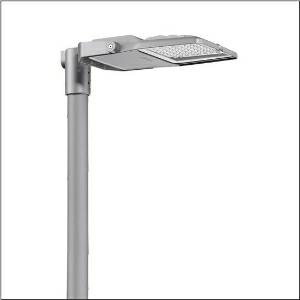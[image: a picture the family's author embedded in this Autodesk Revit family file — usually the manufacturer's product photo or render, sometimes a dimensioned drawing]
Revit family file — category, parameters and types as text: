
# Revit family: floodlight_fl_21_mini___pl52_5xa7775b2d3a_6ba7
name_source: partatom
category: Lighting Fixtures
units: mm (PartAtom-declared; Revit-internal decimal feet)

## family parameters
Cut with Voids When Loaded = No
Host = Face
Light Source = No
Part Type = Normal
Room Calculation Point = No
Round Connector Dimension = Use Diameter
Shared = No

## types (1)
- --- (1 x LED, 6230 lm, 45.7 W, 3000K)
    Apparent Load = 46 VA
    CIE Flux Codes = 26 60 98 100 100
    Color Rendering = 70
    Color Temperature = 3000K
    Default Elevation = 1800 mm
    Description = Floodlight FL 21 mini, floodlight, primary light control with lens, of PMMA, primary optical cover: protective disc, of toughened safety glass, transparent, light distribution: PL52, light emission: direct distribution, installation type: surface-mounted, LED, High Power LED, rated luminous flux: 6.230lm, luminous efficacy: 136lm/W, light colour: 730, colour temperature: 3000K, control gear: Smart Interface (Zhaga), control: flexible luminous flux parameterisation, time-dependent luminous flux control, constant luminous flux control, overheat protection, pre-setting: logarithmic dimming characteristic, with terminal, 6-pole, mains connection: 220..240V, AC, 50/60Hz, start of lifetime: 46W, end of service life: 48W, reduction: 22W, luminaire housing, of diecast aluminium, powder-coated, SITECO metallic grey (DB 702S), corrosivity category C5 mid according to DIN EN ISO 12944, suitable for swimming pools, chlorine-resistant, sealing non-destructively replaceable, please order mast flange separately, mast bracket, of steel, galvanised, powder-coated, SITECO metallic grey (DB 702S), Smart Interface above, protection rating (complete): IP66, insulation class (complete): insulation class II (safety insulation), certification: CE, ENEC, VDE, protection symbol: D, impact resistance: IK08, permissible operating ambient temperature: -40..+40°C, permissible operating ambient temperature for outdoor applications: -40..+50°C, standard: DIN EN 12944, LABS conformity tested according to VDMA 24364:2018-05, packaging unit: 1 piece

Light Distribution: PL52
    Height = 70 mm
    Lamp = 1 x LED
    Lamp Light Flux = 6230 lm
    Lamp Power = 45.7 W
    Lamp count = 1
    Length = 485 mm
    Luminous efficacy = 136 lm/W
    Manufacturer = Siteco
    ModVariant = No
    Model = 5XA7775B2D3A
    Number of Poles = 1
    OnlyDefault = Yes
    Power Factor = 1
    Product Name = Floodlight FL 21 mini | PL52
    Product group = floodlight | pylon annexe
    ProductGroupID = 6201
    Protection Class = Protection class II
    Protection Degree = IP 66
    RLX_Detail_Level = 1
    RLX_Emergency_Light_Flux = 0 lm
    RLX_Emergency_Type = 0
    RLX_Emergency_Type_DB = No
    RlxData = <blob elided: 101253 chars, md5=1d679f04>
    Socket = socket
    Standby Power = 0 W
    System Light Flux = 6230 lm
    System Power = 46 W
    Type Comments = factory setting: luminous flux: 100 % | dim-lin: 254 | 463 mA
    Type Image = l_1007125.jpg
    URL = http://relux.com
    VarID = @adj_162923
    Voltage = 0 V
    Weight = 0.00 kg
    Width = 337 mm

## geometry (parser evidence)
native form markers: Blend x4, Sweep x10
no freeform markers — native parametric forms only
